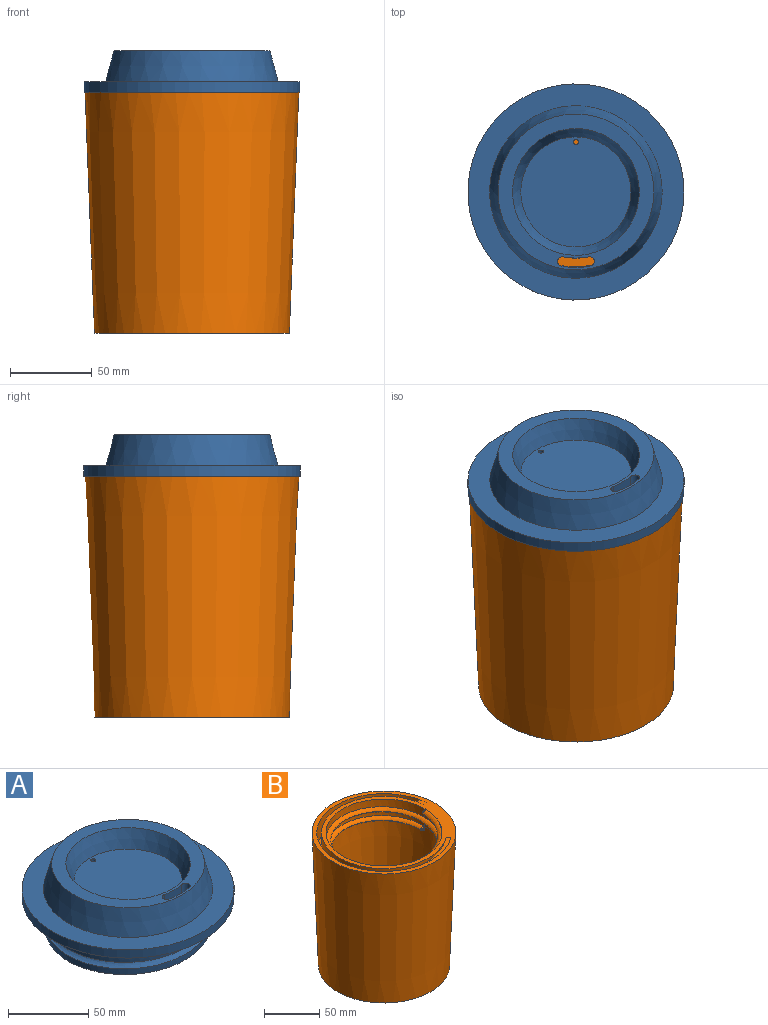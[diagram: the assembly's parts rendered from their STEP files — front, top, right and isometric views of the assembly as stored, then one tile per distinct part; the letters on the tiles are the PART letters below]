
ASSEMBLY  parts=2 mates=1
PART A: 23 faces, bbox 134.9x134.9x55.3 mm
  f0: cylinder r=66.04mm len=132.08mm, axis (0,0,-1), area 2634.9mm2, adj f1,f2
  f1: plane 132.08x132.08mm, normal (0,0,1), area 4974.6mm2, adj f0,f10
  f2: plane 132.08x132.08mm, normal (0,0,-1), area 4974.6mm2, adj f0,f7
  f3: cylinder r=46.35mm len=92.71mm, axis (0,0,1), area 6935.6mm2, adj f4,f5
  f4: plane 105.43x101.97mm, normal (0,0,-1), area 1143.1mm2, adj f3,f8,f18,f19
  f5: plane 92.71x92.71mm, normal (0,0,-1), area 6620.4mm2, adj f3,f13,f14,f15,f16,f17
  f6: plane 95.25x95.25mm, normal (0,0,1), area 2289.7mm2, adj f10,f11,f13,f14,f15,f16
  f7: cone r=52.7mm half-angle=2.5deg, axis (0,0,1), area 1575.4mm2, adj f2,f9,f18,f20,f21
  f8: cone r=52.7mm half-angle=2.5deg, axis (0,0,1), area 1084mm2, adj f4,f9,f18,f19
  f9: cone r=52.7mm half-angle=2.5deg, axis (0,0,1), area 1481.9mm2, adj f7,f8,f18,f19,f22
  f10: cone r=47.62mm half-angle=14.9deg, axis (0,0,-1), area 6214.3mm2, adj f1,f6
  f11: cone r=33.65mm half-angle=21.8deg, axis (0,0,1), area 3110.7mm2, adj f6,f12
  f12: plane 67.31x67.31mm, normal (0,0,1), area 3550.4mm2, adj f11,f17
  f13: cylinder r=40.42mm len=25.4mm, axis (0,0,1), area 392.3mm2, adj f5,f6,f14,f16
  f14: cylinder r=2.86mm len=25.4mm, axis (0,0,1), area 228mm2, adj f5,f6,f13,f15
  f15: cylinder r=46.13mm len=25.4mm, axis (0,0,1), area 468.2mm2, adj f5,f6,f14,f16
  f16: cylinder r=2.86mm len=25.4mm, axis (0,0,1), area 228mm2, adj f5,f6,f13,f15
  f17: cylinder r=1.59mm len=12.7mm, axis (0,0,1), area 126.7mm2, adj f5,f12
  f18: bspline ~105.86x105.68mm, area 3891.7mm2, adj f4,f7,f8,f9,f19,f21
  f19: bspline ~105.86x105.68mm, area 3249.8mm2, adj f4,f8,f9,f18,f21,f22
  f20: plane 2.75x2.48mm, normal (0,-1,0), area 4.5mm2, adj f7,f21,f22
  f21: bspline ~5.11x3.48mm, area 9mm2, adj f7,f18,f19,f20,f22
  f22: bspline ~4.72x3.53mm, area 8mm2, adj f9,f19,f20,f21
PART B: 23 faces, bbox 130.6x130.6x149.5 mm
  f0: bspline ~136.79x122.13mm, area 5800mm2, adj f2,f3,f7,f8
  f1: bspline ~136.79x122.2mm, area 5805mm2, adj f2,f3,f7,f8
  f2: cone r=55.03mm half-angle=2.2deg, axis (0,0,1), area 37836.9mm2, adj f0,f1,f3,f7
  f3: plane 111.55x111.55mm, normal (0,0,1), area 1167.5mm2, adj f0,f1,f2,f8
  f4: cone r=50.8mm half-angle=2.2deg, axis (0,0,1), area 1572.2mm2, adj f5,f7,f13,f16,f19
  f5: cone r=50.8mm half-angle=2.2deg, axis (0,0,1), area 1562.8mm2, adj f4,f6,f11,f14,f16,f17,f20
  f6: cone r=50.8mm half-angle=2.2deg, axis (0,0,1), area 389.2mm2, adj f5,f11,f14
  f7: plane 130.59x130.59mm, normal (0,0,1), area 3420.7mm2, adj f0,f1,f2,f4,f8,f10
  f8: cone r=59.27mm half-angle=2.2deg, axis (0,0,1), area 40816.6mm2, adj f0,f1,f3,f7
  f9: plane 119.02x119.02mm, normal (0,0,-1), area 3017.7mm2, adj f10,f21
  f10: cone r=63.5mm half-angle=2.2deg, axis (0,0,1), area 57806.5mm2, adj f7,f9
  f11: cone r=51.85mm half-angle=3deg, axis (0,0,1), area 36572.6mm2, adj f5,f6,f12,f14,f15,f17,f18
  f12: plane 91.05x91.05mm, normal (0,0,1), area 6511mm2, adj f11
  f13: plane 2.53x2.22mm, normal (0,1,0), area 3.8mm2, adj f4,f19,f20
  f14: bspline ~105.38x105.3mm, area 2992.1mm2, adj f5,f6,f11,f16,f18,f19,f20
  f15: plane 2.51x2.22mm, normal (0,-1,0), area 3.7mm2, adj f11,f17,f18
  f16: bspline ~104.92x104.61mm, area 3119.2mm2, adj f4,f5,f14,f17,f18,f19
  f17: bspline ~4.33x3.15mm, area 8.2mm2, adj f5,f11,f15,f16,f18
  f18: bspline ~4.13x3.18mm, area 8.1mm2, adj f11,f14,f15,f16,f17
  f19: bspline ~4.56x3.33mm, area 8.5mm2, adj f4,f13,f14,f16,f20
  f20: bspline ~4.24x3.16mm, area 7.5mm2, adj f5,f13,f14,f19
  f21: cone r=50.8mm half-angle=3deg, axis (0,0,-1), area 2023mm2, adj f9,f22
  f22: plane 100.93x100.93mm, normal (0,0,-1), area 8001.4mm2, adj f21
PLACE A rot(axis=(0,0,-1),0deg) t=(0,0,45.72)mm
PLACE B at identity fixed
MATE cylindrical A.f0 <-> B.f2  axis (0,0,-1) through (0,0,45.72)mm
